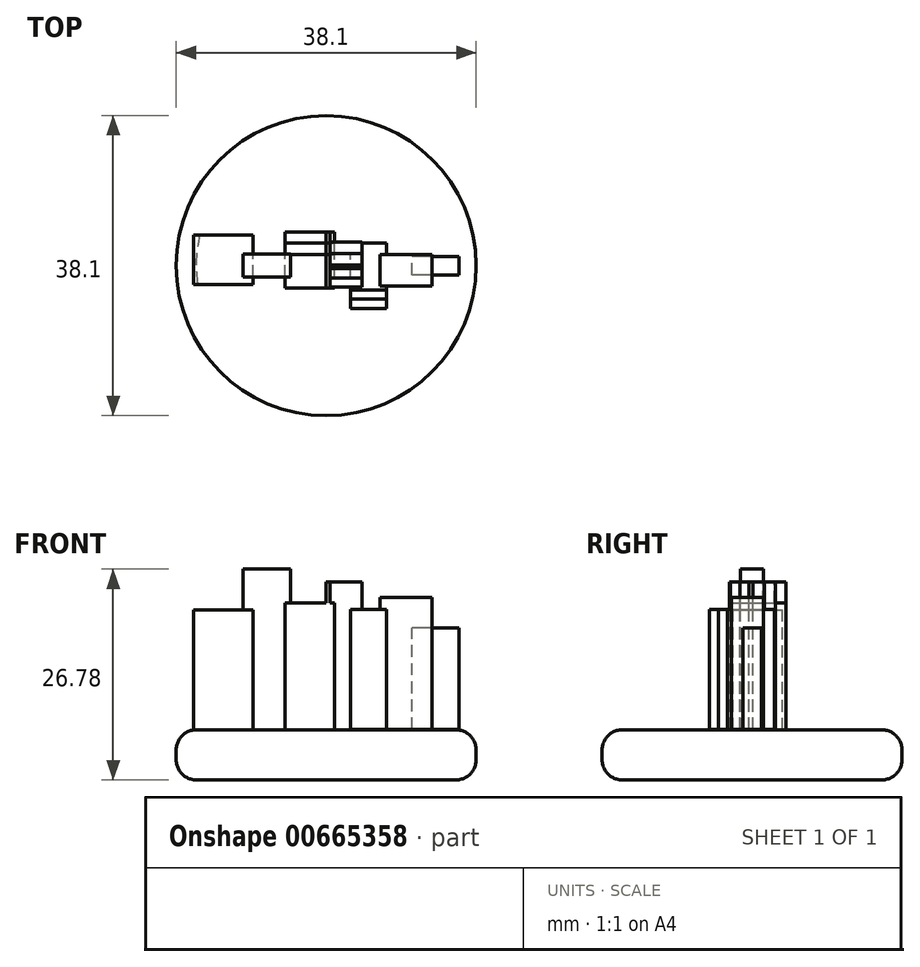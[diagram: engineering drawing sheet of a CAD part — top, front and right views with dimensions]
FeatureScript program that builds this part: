
annotation { "Feature Type Name" : "Feature", "Feature Type Description" : "" }
export const myFeature = defineFeature(function(context is Context, id is Id, definition is map)
    precondition{}
    {
        {
            var Q0;
            Q0=qCreatedBy(makeId("Top.planeOp"),FACE);
            var sketch = newSketch(context, id + "F0", { "sketchPlane" : qUnion([Q0])});
            skCircle(sketch, "E0", {"center": v(-19.05, 0) * mm, "radius": 19.05 * mm});
            skSolve(sketch);
        }
        {
            var Q0;
            Q0 = qSketchRegion(id + "F0", true);
            extrude(context, id + "F1", {"entities" : qUnion([Q0]), "depth" : 6.35 * mm, "offsetDistance" : 25.4 * mm});
        }
        {
            var Q0;
            Q0=makeQuery(id+"F1.opExtrude","CAP_EDGE",EDGE,{"disambiguationData":[OSD([sQuery(id+"F0.wireOp",EDGE,"E0")])],"isStart":false});
            var Q1;
            Q1=makeQuery(id+"F1.opExtrude","CAP_EDGE",EDGE,{"disambiguationData":[OSD([sQuery(id+"F0.wireOp",EDGE,"E0")])],"isStart":true});
            fillet(context, id + "F2", {"entities" : qUnion([Q0, Q1]), "radius" : 2.54 * mm, "tangentPropagation" : true, "allowEdgeOverflow" : false});
        }
        {
            var Q0;
            Q0=qCreatedBy(makeId("Front.planeOp"),FACE);
            var sketch = newSketch(context, id + "F3", { "sketchPlane" : qUnion([Q0])});
            skLineSegment(sketch, "E1.bottom", {"start": v(-35.93, 6.35) * mm, "end": v(-28.3, 6.35) * mm});
            skLineSegment(sketch, "E1.top", {"start": v(-35.93, 21.59) * mm, "end": v(-28.3, 21.59) * mm});
            skLineSegment(sketch, "E1.left", {"start": v(-35.93, 6.35) * mm, "end": v(-35.93, 21.59) * mm});
            skLineSegment(sketch, "E1.right", {"start": v(-28.3, 6.35) * mm, "end": v(-28.3, 21.59) * mm});
            skLineSegment(sketch, "E2.bottom", {"start": v(-29.6, 6.35) * mm, "end": v(-23.58, 6.35) * mm});
            skLineSegment(sketch, "E2.top", {"start": v(-29.6, 26.78) * mm, "end": v(-23.58, 26.78) * mm});
            skLineSegment(sketch, "E2.left", {"start": v(-29.6, 6.35) * mm, "end": v(-29.6, 26.78) * mm});
            skLineSegment(sketch, "E2.right", {"start": v(-23.58, 6.35) * mm, "end": v(-23.58, 26.78) * mm});
            skLineSegment(sketch, "E3.bottom", {"start": v(-2.19, 6.41) * mm, "end": v(-8.13, 6.41) * mm});
            skLineSegment(sketch, "E3.top", {"start": v(-2.19, 19.31) * mm, "end": v(-8.13, 19.31) * mm});
            skLineSegment(sketch, "E3.left", {"start": v(-2.19, 6.41) * mm, "end": v(-2.19, 19.31) * mm});
            skLineSegment(sketch, "E3.right", {"start": v(-8.13, 6.41) * mm, "end": v(-8.13, 19.31) * mm});
            skLineSegment(sketch, "E4.bottom", {"start": v(-5.58, 6.41) * mm, "end": v(-12.2, 6.41) * mm});
            skLineSegment(sketch, "E4.top", {"start": v(-5.58, 23.18) * mm, "end": v(-12.2, 23.18) * mm});
            skLineSegment(sketch, "E4.left", {"start": v(-5.58, 6.41) * mm, "end": v(-5.58, 23.18) * mm});
            skLineSegment(sketch, "E4.right", {"start": v(-12.2, 6.41) * mm, "end": v(-12.2, 23.18) * mm});
            skLineSegment(sketch, "E5.bottom", {"start": v(-11.36, 6.41) * mm, "end": v(-15.94, 6.41) * mm});
            skLineSegment(sketch, "E5.top", {"start": v(-11.36, 21.65) * mm, "end": v(-15.94, 21.65) * mm});
            skLineSegment(sketch, "E5.left", {"start": v(-11.36, 6.41) * mm, "end": v(-11.36, 21.65) * mm});
            skLineSegment(sketch, "E5.right", {"start": v(-15.94, 6.41) * mm, "end": v(-15.94, 21.65) * mm});
            skLineSegment(sketch, "E6.bottom", {"start": v(-24.3, 6.35) * mm, "end": v(-17.98, 6.35) * mm});
            skLineSegment(sketch, "E6.top", {"start": v(-24.3, 22.47) * mm, "end": v(-17.98, 22.47) * mm});
            skLineSegment(sketch, "E6.left", {"start": v(-24.3, 6.35) * mm, "end": v(-24.3, 22.47) * mm});
            skLineSegment(sketch, "E6.right", {"start": v(-17.98, 6.35) * mm, "end": v(-17.98, 22.47) * mm});
            skLineSegment(sketch, "E7.bottom", {"start": v(-19.04, 6.35) * mm, "end": v(-14.5, 6.35) * mm});
            skLineSegment(sketch, "E7.top", {"start": v(-19.04, 25.17) * mm, "end": v(-14.5, 25.17) * mm});
            skLineSegment(sketch, "E7.left", {"start": v(-19.04, 6.35) * mm, "end": v(-19.04, 25.17) * mm});
            skLineSegment(sketch, "E7.right", {"start": v(-14.5, 6.35) * mm, "end": v(-14.5, 25.17) * mm});
            skLineSegment(sketch, "E8.bottom", {"start": v(-23.58, 22.47) * mm, "end": v(-18.54, 22.47) * mm});
            skLineSegment(sketch, "E8.top", {"start": v(-23.58, 25.46) * mm, "end": v(-18.54, 25.46) * mm});
            skLineSegment(sketch, "E8.left", {"start": v(-23.58, 22.47) * mm, "end": v(-23.58, 25.46) * mm});
            skLineSegment(sketch, "E8.right", {"start": v(-18.54, 22.47) * mm, "end": v(-18.54, 25.46) * mm});
            skLineSegment(sketch, "E9.bottom", {"start": v(-22.96, 25.46) * mm, "end": v(-19.3, 25.46) * mm});
            skLineSegment(sketch, "E9.top", {"start": v(-22.96, 28.36) * mm, "end": v(-19.3, 28.36) * mm});
            skLineSegment(sketch, "E9.left", {"start": v(-22.96, 25.46) * mm, "end": v(-22.96, 28.36) * mm});
            skLineSegment(sketch, "E9.right", {"start": v(-19.3, 25.46) * mm, "end": v(-19.3, 28.36) * mm});
            skLineSegment(sketch, "E10.bottom", {"start": v(-22.4, 28.36) * mm, "end": v(-19.7, 28.36) * mm});
            skLineSegment(sketch, "E10.top", {"start": v(-22.4, 30.57) * mm, "end": v(-19.7, 30.57) * mm});
            skLineSegment(sketch, "E10.left", {"start": v(-22.4, 28.36) * mm, "end": v(-22.4, 30.57) * mm});
            skLineSegment(sketch, "E10.right", {"start": v(-19.7, 28.36) * mm, "end": v(-19.7, 30.57) * mm});
            skLineSegment(sketch, "E11.bottom", {"start": v(-21.3, 30.57) * mm, "end": v(-20.8, 30.57) * mm});
            skLineSegment(sketch, "E11.top", {"start": v(-21.3, 36) * mm, "end": v(-20.8, 36) * mm});
            skLineSegment(sketch, "E11.left", {"start": v(-21.3, 30.57) * mm, "end": v(-21.3, 36) * mm});
            skLineSegment(sketch, "E11.right", {"start": v(-20.8, 30.57) * mm, "end": v(-20.8, 36) * mm});
            skSolve(sketch);
        }
        {
            var Q0;
            {var subQ0=sQuery(id+"F3.wireOp",EDGE,"E1.bottom");Q0=makeQuery(id+"F3.imprint","IMPRINT",FACE,{"disambiguationData":[TD([[makeQuery(id+"F3.imprint","IMPRINT",EDGE,{"derivedFrom":subQ0}),1.0]])]});}
            var Q1;
            {var subQ0=sQuery(id+"F3.wireOp",EDGE,"E1.right");Q1=makeQuery(id+"F3.imprint","IMPRINT",FACE,{"disambiguationData":[TD([[makeQuery(id+"F3.imprint","IMPRINT",EDGE,{"derivedFrom":subQ0}),1.0]])]});}
            extrude(context, id + "F4", {"entities" : qUnion([Q0, Q1]), "operationType" : NewBodyOperationType.ADD, "endBound" : BoundingType.SYMMETRIC, "depth" : 4.83 * mm, "offsetDistance" : 25.4 * mm});
        }
        {
            var Q0;
            {var subQ0=sQuery(id+"F3.wireOp",EDGE,"E6.bottom");var subQ1=sQuery(id+"F3.wireOp",EDGE,"E2.right");var subQ2=makeQuery(id+"F3.imprint","INTERSECT",VERTEX,{"derivedFrom":[subQ1,subQ0]});Q0=makeQuery(id+"F3.imprint","IMPRINT",FACE,{"disambiguationData":[TD([[makeQuery(id+"F3.imprint","IMPRINT",EDGE,{"disambiguationData":[TD([[subQ2,-1.0]])],"derivedFrom":subQ0}),1.0]])]});}
            var Q1;
            {var subQ3=sQuery(id+"F3.wireOp",EDGE,"E6.right");Q1=makeQuery(id+"F3.imprint","IMPRINT",FACE,{"disambiguationData":[TD([[makeQuery(id+"F3.imprint","IMPRINT",EDGE,{"derivedFrom":subQ3}),1.0]])]});}
            var Q2;
            {var subQ5=sQuery(id+"F3.wireOp",EDGE,"E6.left");Q2=makeQuery(id+"F3.imprint","IMPRINT",FACE,{"disambiguationData":[TD([[makeQuery(id+"F3.imprint","IMPRINT",EDGE,{"derivedFrom":subQ5}),-1.0]])]});}
            var Q3;
            {var subQ0=sQuery(id+"F3.wireOp",EDGE,"E8.left");Q3=makeQuery(id+"F3.imprint","IMPRINT",FACE,{"disambiguationData":[TD([[makeQuery(id+"F3.imprint","IMPRINT",EDGE,{"derivedFrom":subQ0}),-1.0]])]});}
            var Q4;
            {var subQ0=sQuery(id+"F3.wireOp",EDGE,"E7.left");var subQ1=sQuery(id+"F3.wireOp",EDGE,"E7.top");var subQ2=makeQuery(id+"F3.imprint","INTERSECT",VERTEX,{"derivedFrom":[subQ1,subQ0]});Q4=makeQuery(id+"F3.imprint","IMPRINT",FACE,{"disambiguationData":[TD([[makeQuery(id+"F3.imprint","IMPRINT",EDGE,{"disambiguationData":[TD([[subQ2,-1.0]])],"derivedFrom":subQ1}),-1.0]])]});}
            var Q5;
            Q5=makeQuery(id+"F3.imprint","IMPRINT",FACE,{"disambiguationData":[TD([[makeQuery(id+"F3.imprint","IMPRINT",EDGE,{"derivedFrom":sQuery(id+"F3.wireOp",EDGE,"E9.bottom")}),1.0]])]});
            var Q6;
            Q6=makeQuery(id+"F3.imprint","IMPRINT",FACE,{"disambiguationData":[TD([[makeQuery(id+"F3.imprint","IMPRINT",EDGE,{"derivedFrom":sQuery(id+"F3.wireOp",EDGE,"E10.bottom")}),1.0]])]});
            var Q7;
            Q7=makeQuery(id+"F3.imprint","IMPRINT",FACE,{"disambiguationData":[TD([[makeQuery(id+"F3.imprint","IMPRINT",EDGE,{"derivedFrom":sQuery(id+"F3.wireOp",EDGE,"E11.bottom")}),1.0]])]});
            extrude(context, id + "F5", {"entities" : qUnion([Q0, Q1, Q2, Q3, Q4, Q5, Q6, Q7]), "operationType" : NewBodyOperationType.ADD, "endBound" : BoundingType.SYMMETRIC, "depth" : 2.6 * mm, "offsetDistance" : 25.4 * mm});
        }
        {
            var Q0;
            {var subQ0=sQuery(id+"F3.wireOp",EDGE,"E5.bottom");var subQ1=sQuery(id+"F3.wireOp",EDGE,"E4.right");var subQ2=makeQuery(id+"F3.imprint","INTERSECT",VERTEX,{"derivedFrom":[subQ1,subQ0]});Q0=makeQuery(id+"F3.imprint","IMPRINT",FACE,{"disambiguationData":[TD([[makeQuery(id+"F3.imprint","IMPRINT",EDGE,{"disambiguationData":[TD([[subQ2,-1.0]])],"derivedFrom":subQ1}),1.0]])]});}
            var Q1;
            {var subQ0=sQuery(id+"F3.wireOp",EDGE,"E5.right");Q1=makeQuery(id+"F3.imprint","IMPRINT",FACE,{"disambiguationData":[TD([[makeQuery(id+"F3.imprint","IMPRINT",EDGE,{"derivedFrom":subQ0}),-1.0]])]});}
            var Q2;
            {var subQ5=sQuery(id+"F3.wireOp",EDGE,"E5.left");Q2=makeQuery(id+"F3.imprint","IMPRINT",FACE,{"disambiguationData":[TD([[makeQuery(id+"F3.imprint","IMPRINT",EDGE,{"derivedFrom":subQ5}),1.0]])]});}
            extrude(context, id + "F6", {"entities" : qUnion([Q0, Q1, Q2]), "endBound" : BoundingType.SYMMETRIC, "depth" : 2.6 * mm, "offsetDistance" : 25.4 * mm});
        }
        {
            var Q0;
            {var subQ1=sQuery(id+"F3.wireOp",EDGE,"E3.right");Q0=makeQuery(id+"F3.imprint","IMPRINT",FACE,{"disambiguationData":[TD([[makeQuery(id+"F3.imprint","IMPRINT",EDGE,{"derivedFrom":subQ1}),1.0]])]});}
            var Q1;
            {var subQ0=sQuery(id+"F3.wireOp",EDGE,"E3.right");Q1=makeQuery(id+"F3.imprint","IMPRINT",FACE,{"disambiguationData":[TD([[makeQuery(id+"F3.imprint","IMPRINT",EDGE,{"derivedFrom":subQ0}),-1.0]])]});}
            var Q2;
            Q2=makeQuery(id+"F6.opExtrude","CAP_FACE",FACE,{"disambiguationData":[OSD([sQuery(id+"F3.wireOp",EDGE,"E5.bottom"),sQuery(id+"F3.wireOp",EDGE,"E5.top"),sQuery(id+"F3.wireOp",EDGE,"E5.left"),sQuery(id+"F3.wireOp",EDGE,"E5.right")])],"isStart":false});
            extrude(context, id + "F7", {"entities" : qUnion([Q0, Q1, Q2]), "operationType" : NewBodyOperationType.ADD, "endBound" : BoundingType.SYMMETRIC, "depth" : 2.84 * mm, "offsetDistance" : 25.4 * mm});
        }
        {
            var Q0;
            {var subQ9=sQuery(id+"F3.wireOp",EDGE,"E5.right");Q0=makeQuery(id+"F3.imprint","IMPRINT",FACE,{"disambiguationData":[TD([[makeQuery(id+"F3.imprint","IMPRINT",EDGE,{"derivedFrom":subQ9}),1.0]])]});}
            var Q1;
            Q1=makeQuery(id+"F7.opExtrude","CAP_FACE",FACE,{"disambiguationData":[OSD([sQuery(id+"F3.wireOp",EDGE,"E5.bottom"),sQuery(id+"F3.wireOp",EDGE,"E5.top"),sQuery(id+"F3.wireOp",EDGE,"E5.left"),sQuery(id+"F3.wireOp",EDGE,"E5.right")])],"isStart":false});
            var Q2;
            Q2=makeQuery(id+"F5.opExtrude","CAP_FACE",FACE,{"disambiguationData":[OSD([sQuery(id+"F3.wireOp",EDGE,"E6.bottom"),sQuery(id+"F3.wireOp",EDGE,"E6.top"),sQuery(id+"F3.wireOp",EDGE,"E6.left"),sQuery(id+"F3.wireOp",EDGE,"E6.right"),sQuery(id+"F3.wireOp",EDGE,"E7.bottom"),sQuery(id+"F3.wireOp",EDGE,"E8.top"),sQuery(id+"F3.wireOp",EDGE,"E8.left"),sQuery(id+"F3.wireOp",EDGE,"E8.right"),sQuery(id+"F3.wireOp",EDGE,"E9.top"),sQuery(id+"F3.wireOp",EDGE,"E9.left"),sQuery(id+"F3.wireOp",EDGE,"E9.right"),sQuery(id+"F3.wireOp",EDGE,"E10.top"),sQuery(id+"F3.wireOp",EDGE,"E10.left"),sQuery(id+"F3.wireOp",EDGE,"E10.right"),sQuery(id+"F3.wireOp",EDGE,"E11.top"),sQuery(id+"F3.wireOp",EDGE,"E11.left"),sQuery(id+"F3.wireOp",EDGE,"E11.right")])],"isStart":false});
            var Q3;
            Q3=makeQuery(id+"F6.opExtrude","CAP_FACE",FACE,{"disambiguationData":[OSD([sQuery(id+"F3.wireOp",EDGE,"E5.bottom"),sQuery(id+"F3.wireOp",EDGE,"E5.top"),sQuery(id+"F3.wireOp",EDGE,"E5.left"),sQuery(id+"F3.wireOp",EDGE,"E5.right")])],"isStart":true});
            var Q4;
            Q4=makeQuery(id+"F5.opExtrude","CAP_FACE",FACE,{"disambiguationData":[OSD([sQuery(id+"F3.wireOp",EDGE,"E6.bottom"),sQuery(id+"F3.wireOp",EDGE,"E6.top"),sQuery(id+"F3.wireOp",EDGE,"E6.left"),sQuery(id+"F3.wireOp",EDGE,"E6.right"),sQuery(id+"F3.wireOp",EDGE,"E7.bottom"),sQuery(id+"F3.wireOp",EDGE,"E8.top"),sQuery(id+"F3.wireOp",EDGE,"E8.left"),sQuery(id+"F3.wireOp",EDGE,"E8.right"),sQuery(id+"F3.wireOp",EDGE,"E9.top"),sQuery(id+"F3.wireOp",EDGE,"E9.left"),sQuery(id+"F3.wireOp",EDGE,"E9.right"),sQuery(id+"F3.wireOp",EDGE,"E10.top"),sQuery(id+"F3.wireOp",EDGE,"E10.left"),sQuery(id+"F3.wireOp",EDGE,"E10.right"),sQuery(id+"F3.wireOp",EDGE,"E11.top"),sQuery(id+"F3.wireOp",EDGE,"E11.left"),sQuery(id+"F3.wireOp",EDGE,"E11.right")])],"isStart":true});
            extrude(context, id + "F8", {"entities" : qUnion([Q0, Q1, Q2, Q3, Q4]), "endBound" : BoundingType.SYMMETRIC, "depth" : 3.1 * mm, "offsetDistance" : 25.4 * mm});
        }
        {
            var Q0;
            {var subQ1=sQuery(id+"F3.wireOp",EDGE,"E1.right");Q0=makeQuery(id+"F3.imprint","IMPRINT",FACE,{"disambiguationData":[TD([[makeQuery(id+"F3.imprint","IMPRINT",EDGE,{"derivedFrom":subQ1}),-1.0]])]});}
            var Q1;
            Q1=makeQuery(id+"F4.opExtrude","CAP_FACE",FACE,{"disambiguationData":[OSD([sQuery(id+"F3.wireOp",EDGE,"E1.bottom"),sQuery(id+"F3.wireOp",EDGE,"E1.top"),sQuery(id+"F3.wireOp",EDGE,"E1.left"),sQuery(id+"F3.wireOp",EDGE,"E1.right"),sQuery(id+"F3.wireOp",EDGE,"E2.bottom")])],"isStart":true});
            var Q2;
            {var subQ0=sQuery(id+"F3.wireOp",EDGE,"E11.right");var subQ1=sQuery(id+"F3.wireOp",EDGE,"E11.left");var subQ2=sQuery(id+"F3.wireOp",EDGE,"E11.top");var subQ3=sQuery(id+"F3.wireOp",EDGE,"E10.right");var subQ4=sQuery(id+"F3.wireOp",EDGE,"E10.left");var subQ5=sQuery(id+"F3.wireOp",EDGE,"E10.top");var subQ6=sQuery(id+"F3.wireOp",EDGE,"E9.right");var subQ7=sQuery(id+"F3.wireOp",EDGE,"E9.left");var subQ8=sQuery(id+"F3.wireOp",EDGE,"E9.top");var subQ9=sQuery(id+"F3.wireOp",EDGE,"E8.right");var subQ10=sQuery(id+"F3.wireOp",EDGE,"E8.left");var subQ11=sQuery(id+"F3.wireOp",EDGE,"E8.top");var subQ12=sQuery(id+"F3.wireOp",EDGE,"E7.bottom");var subQ13=sQuery(id+"F3.wireOp",EDGE,"E6.right");var subQ14=sQuery(id+"F3.wireOp",EDGE,"E6.left");var subQ15=sQuery(id+"F3.wireOp",EDGE,"E6.top");var subQ16=sQuery(id+"F3.wireOp",EDGE,"E6.bottom");Q2=makeQuery(id+"F8.opExtrude","CAP_FACE",FACE,{"disambiguationData":[OSD([subQ16,subQ15,subQ14,subQ13,subQ12,subQ11,subQ10,subQ9,subQ8,subQ7,subQ6,subQ5,subQ4,subQ3,subQ2,subQ1,subQ0]),TDD([makeQuery(id+"F5.opExtrude","CAP_FACE",FACE,{"disambiguationData":[OSD([subQ16,subQ15,subQ14,subQ13,subQ12,subQ11,subQ10,subQ9,subQ8,subQ7,subQ6,subQ5,subQ4,subQ3,subQ2,subQ1,subQ0])],"isStart":true})])],"isStart":true});}
            extrude(context, id + "F9", {"entities" : qUnion([Q0, Q1, Q2]), "endBound" : BoundingType.SYMMETRIC, "depth" : 2.9 * mm, "offsetDistance" : 25.4 * mm});
        }
        {
            var Q0;
            {var subQ0=sQuery(id+"F3.wireOp",EDGE,"E3.bottom");Q0=makeQuery(id+"F3.imprint","IMPRINT",FACE,{"disambiguationData":[TD([[makeQuery(id+"F3.imprint","IMPRINT",EDGE,{"derivedFrom":subQ0}),-1.0]])]});}
            var Q1;
            Q1=makeQuery(id+"F7.opExtrude","CAP_FACE",FACE,{"disambiguationData":[OSD([sQuery(id+"F3.wireOp",EDGE,"E4.bottom"),sQuery(id+"F3.wireOp",EDGE,"E4.top"),sQuery(id+"F3.wireOp",EDGE,"E4.left"),sQuery(id+"F3.wireOp",EDGE,"E4.right"),sQuery(id+"F3.wireOp",EDGE,"E5.top"),sQuery(id+"F3.wireOp",EDGE,"E5.left")])],"isStart":false});
            var Q2;
            {var subQ0=sQuery(id+"F3.wireOp",EDGE,"E5.right");var subQ1=sQuery(id+"F3.wireOp",EDGE,"E5.left");var subQ2=sQuery(id+"F3.wireOp",EDGE,"E5.top");var subQ3=sQuery(id+"F3.wireOp",EDGE,"E5.bottom");Q2=makeQuery(id+"F8.opExtrude","CAP_FACE",FACE,{"disambiguationData":[OSD([subQ3,subQ2,subQ1,subQ0]),TDD([makeQuery(id+"F7.opExtrude","CAP_FACE",FACE,{"disambiguationData":[OSD([subQ3,subQ2,subQ1,subQ0])],"isStart":false})])],"isStart":false});}
            extrude(context, id + "F10", {"entities" : qUnion([Q0, Q1, Q2]), "endBound" : BoundingType.SYMMETRIC, "depth" : 2.34 * mm, "offsetDistance" : 25.4 * mm});
        }
    });
